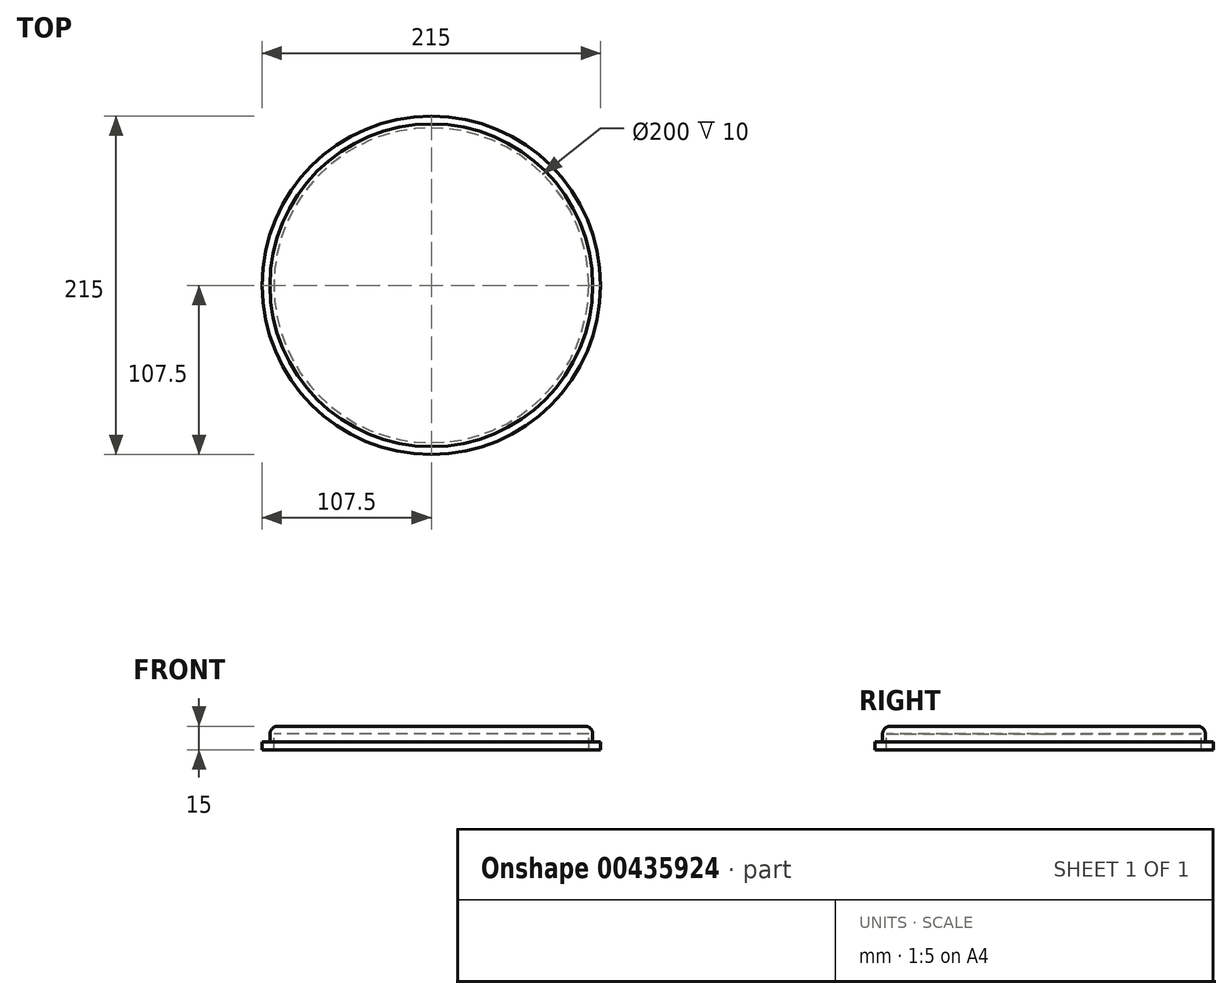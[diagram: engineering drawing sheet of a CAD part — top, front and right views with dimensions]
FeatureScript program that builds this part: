
annotation { "Feature Type Name" : "Feature", "Feature Type Description" : "" }
export const myFeature = defineFeature(function(context is Context, id is Id, definition is map)
    precondition{}
    {
        {
            var Q0;
            Q0=qCreatedBy(makeId("Top.planeOp"),FACE);
            var sketch = newSketch(context, id + "F0", { "sketchPlane" : qUnion([Q0])});
            skCircle(sketch, "E0", {"center": v(0, 0) * mm, "radius": 107.5 * mm});
            skSolve(sketch);
        }
        {
            var Q0;
            Q0=makeQuery(id+"F0.imprint","IMPRINT",FACE,{"disambiguationData":[TD([[makeQuery(id+"F0.imprint","IMPRINT",EDGE,{"derivedFrom":sQuery(id+"F0.wireOp",EDGE,"E0")}),1.0]])]});
            extrude(context, id + "F1", {"entities" : qUnion([Q0]), "depth" : 5 * mm});
        }
        {
            var Q0;
            Q0=makeQuery(id+"F1.opExtrude","CAP_FACE",FACE,{"disambiguationData":[OSD([sQuery(id+"F0.wireOp",EDGE,"E0")])],"isStart":false});
            var sketch = newSketch(context, id + "F2", { "sketchPlane" : qUnion([Q0])});
            skCircle(sketch, "E1", {"center": v(0, 0) * mm, "radius": 100 * mm});
            skSolve(sketch);
        }
        {
            var Q0;
            Q0 = qSketchRegion(id + "F2", true);
            extrude(context, id + "F3", {"entities" : qUnion([Q0]), "operationType" : NewBodyOperationType.REMOVE, "oppositeDirection" : true, "depth" : 6 * mm});
        }
        {
            var Q0;
            Q0=makeQuery(id+"F1.opExtrude","CAP_FACE",FACE,{"disambiguationData":[OSD([sQuery(id+"F0.wireOp",EDGE,"E0")])],"isStart":false});
            var sketch = newSketch(context, id + "F4", { "sketchPlane" : qUnion([Q0])});
            skCircle(sketch, "E2", {"center": v(0, 0) * mm, "radius": 100 * mm});
            skCircle(sketch, "E3", {"center": v(0, 0) * mm, "radius": 102.5 * mm});
            skSolve(sketch);
        }
        {
            var Q0;
            Q0=makeQuery(id+"F4.imprint","IMPRINT",FACE,{"disambiguationData":[TD([[makeQuery(id+"F4.imprint","IMPRINT",EDGE,{"derivedFrom":sQuery(id+"F4.wireOp",EDGE,"E2")}),-1.0]])]});
            extrude(context, id + "F5", {"entities" : qUnion([Q0]), "operationType" : NewBodyOperationType.ADD, "depth" : 5 * mm});
        }
        {
            var Q0;
            Q0=makeQuery(id+"F5.opExtrude","CAP_FACE",FACE,{"disambiguationData":[OSD([sQuery(id+"F4.wireOp",EDGE,"E2"),sQuery(id+"F4.wireOp",EDGE,"E3")])],"isStart":false});
            var sketch = newSketch(context, id + "F6", { "sketchPlane" : qUnion([Q0])});
            skCircle(sketch, "E4", {"center": v(0, 0) * mm, "radius": 102.5 * mm});
            skSolve(sketch);
        }
        {
            var Q0;
            Q0 = qSketchRegion(id + "F6", true);
            extrude(context, id + "F7", {"entities" : qUnion([Q0]), "operationType" : NewBodyOperationType.ADD, "depth" : 5 * mm});
        }
        {
            var Q0;
            Q0=makeQuery(id+"F7.opExtrude","CAP_EDGE",EDGE,{"disambiguationData":[OSD([sQuery(id+"F6.wireOp",EDGE,"E4")])],"isStart":false});
            fillet(context, id + "F8", {"entities" : qUnion([Q0]), "radius" : 5 * mm, "tangentPropagation" : true, "allowEdgeOverflow" : false});
        }
    });
